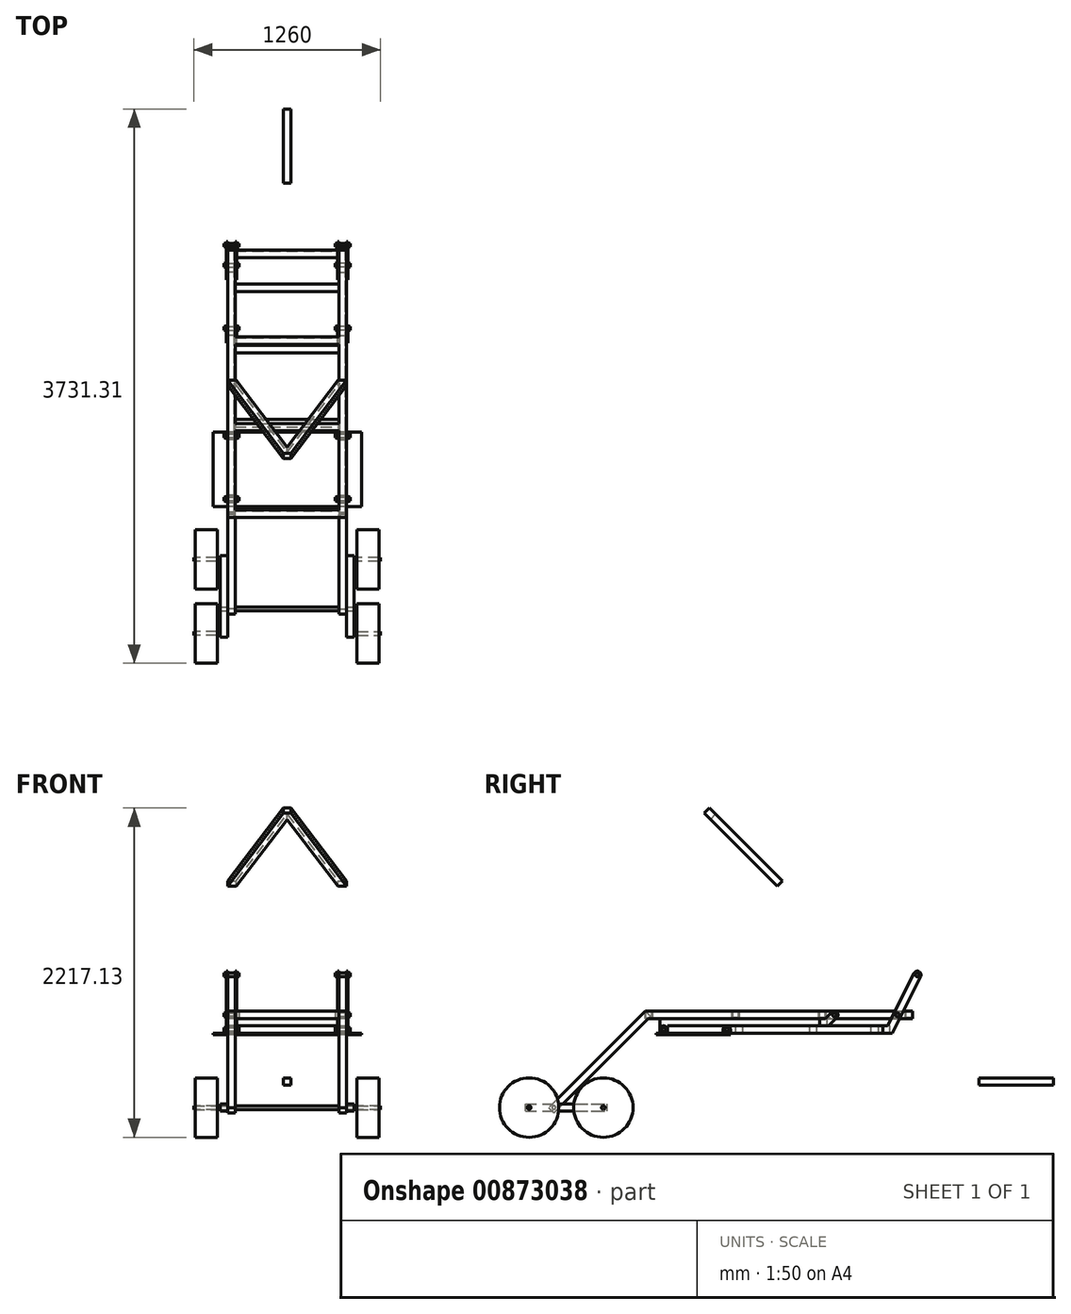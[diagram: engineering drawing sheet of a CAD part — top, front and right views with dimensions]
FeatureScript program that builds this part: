
annotation { "Feature Type Name" : "Feature", "Feature Type Description" : "" }
export const myFeature = defineFeature(function(context is Context, id is Id, definition is map)
    precondition{}
    {
        {
            assignVariable(context, id + "F0", {"name" : "TopLength", "anyValue" : 1800});
        }
        {
            assignVariable(context, id + "F1", {"name" : "TopWidth", "anyValue" : 800});
        }
        {
            assignVariable(context, id + "F2", {"name" : "PipeWidth", "anyValue" : 50});
        }
        {
            assignVariable(context, id + "F3", {"name" : "PipeThickness", "anyValue" : 5});
        }
        {
            var Q0;
            Q0=qCreatedBy(makeId("Front.planeOp"),FACE);
            var sketch = newSketch(context, id + "F4", { "sketchPlane" : qUnion([Q0])});
            skLineSegment(sketch, "E0.bottom", {"start": v(400, -25) * mm, "end": v(350, -25) * mm});
            skLineSegment(sketch, "E0.top", {"start": v(400, 25) * mm, "end": v(350, 25) * mm});
            skLineSegment(sketch, "E0.left", {"start": v(400, -25) * mm, "end": v(400, 25) * mm});
            skLineSegment(sketch, "E0.right", {"start": v(350, -25) * mm, "end": v(350, 25) * mm});
            skPoint(sketch, "E0.middle", {"position": v(375, 0) * mm});
            skSolve(sketch);
        }
        {
            var Q0;
            Q0 = qSketchRegion(id + "F4", true);
            extrude(context, id + "F5", {"entities" : qUnion([Q0]), "endBound" : BoundingType.SYMMETRIC, "depth" : (getVariable(context, 'TopLength')) * mm, "offsetDistance" : 25 * mm});
        }
        {
            var Q0;
            Q0=makeQuery(id+"F5.opExtrude","CAP_FACE",FACE,{"disambiguationData":[OSD([sQuery(id+"F4.wireOp",EDGE,"E0.bottom"),sQuery(id+"F4.wireOp",EDGE,"E0.top"),sQuery(id+"F4.wireOp",EDGE,"E0.left"),sQuery(id+"F4.wireOp",EDGE,"E0.right")])],"isStart":false});
            var Q1;
            Q1=makeQuery(id+"F5.opExtrude","CAP_FACE",FACE,{"disambiguationData":[OSD([sQuery(id+"F4.wireOp",EDGE,"E0.bottom"),sQuery(id+"F4.wireOp",EDGE,"E0.top"),sQuery(id+"F4.wireOp",EDGE,"E0.left"),sQuery(id+"F4.wireOp",EDGE,"E0.right")])],"isStart":true});
            shell(context, id + "F6", {"entities" : qUnion([Q0, Q1]), "thickness" : (getVariable(context, 'PipeThickness')) * mm});
        }
        {
            var Q0;
            Q0=makeQuery(id+"F5.opExtrude","SWEPT_BODY",BODY,{"disambiguationData":[OSD([sQuery(id+"F4.wireOp",EDGE,"E0.bottom"),sQuery(id+"F4.wireOp",EDGE,"E0.top"),sQuery(id+"F4.wireOp",EDGE,"E0.left"),sQuery(id+"F4.wireOp",EDGE,"E0.right")])]});
            var Q1;
            Q1=qCreatedBy(makeId("Right.planeOp"),FACE);
            mirror(context, id + "F7", {"entities" : qUnion([Q0]), "mirrorPlane" : qUnion([Q1])});
        }
        {
            var Q0;
            Q0=makeQuery(id+"F5.opExtrude","SWEPT_FACE",FACE,{"disambiguationData":[OSD([sQuery(id+"F4.wireOp",EDGE,"E0.right")])]});
            var sketch = newSketch(context, id + "F8", { "sketchPlane" : qUnion([Q0])});
            skLineSegment(sketch, "E1.bottom", {"start": v(900, 25) * mm, "end": v(850, 25) * mm});
            skLineSegment(sketch, "E1.top", {"start": v(900, -25) * mm, "end": v(850, -25) * mm});
            skLineSegment(sketch, "E1.left", {"start": v(900, 25) * mm, "end": v(900, -25) * mm});
            skLineSegment(sketch, "E1.right", {"start": v(850, 25) * mm, "end": v(850, -25) * mm});
            skLineSegment(sketch, "E2.bottom", {"start": v(855, 20) * mm, "end": v(895, 20) * mm});
            skLineSegment(sketch, "E2.top", {"start": v(855, -20) * mm, "end": v(895, -20) * mm});
            skLineSegment(sketch, "E2.left", {"start": v(855, 20) * mm, "end": v(855, -20) * mm});
            skLineSegment(sketch, "E2.right", {"start": v(895, 20) * mm, "end": v(895, -20) * mm});
            skLineSegment(sketch, "E3.1.0.0", {"start": v(271.67, -20) * mm, "end": v(311.67, -20) * mm});
            skLineSegment(sketch, "E3.1.0.1", {"start": v(311.67, 20) * mm, "end": v(311.67, -20) * mm});
            skLineSegment(sketch, "E3.1.0.2", {"start": v(316.67, 25) * mm, "end": v(266.67, 25) * mm});
            skLineSegment(sketch, "E3.1.0.3", {"start": v(316.67, 25) * mm, "end": v(316.67, -25) * mm});
            skLineSegment(sketch, "E3.1.0.4", {"start": v(271.67, 20) * mm, "end": v(311.67, 20) * mm});
            skLineSegment(sketch, "E3.1.0.5", {"start": v(316.67, -25) * mm, "end": v(266.67, -25) * mm});
            skLineSegment(sketch, "E3.1.0.6", {"start": v(271.67, 20) * mm, "end": v(271.67, -20) * mm});
            skLineSegment(sketch, "E3.1.0.7", {"start": v(266.67, 25) * mm, "end": v(266.67, -25) * mm});
            skLineSegment(sketch, "E3.2.0.0", {"start": v(-311.67, -20) * mm, "end": v(-271.67, -20) * mm});
            skLineSegment(sketch, "E3.2.0.1", {"start": v(-271.67, 20) * mm, "end": v(-271.67, -20) * mm});
            skLineSegment(sketch, "E3.2.0.2", {"start": v(-266.67, 25) * mm, "end": v(-316.67, 25) * mm});
            skLineSegment(sketch, "E3.2.0.3", {"start": v(-266.67, 25) * mm, "end": v(-266.67, -25) * mm});
            skLineSegment(sketch, "E3.2.0.4", {"start": v(-311.67, 20) * mm, "end": v(-271.67, 20) * mm});
            skLineSegment(sketch, "E3.2.0.5", {"start": v(-266.67, -25) * mm, "end": v(-316.67, -25) * mm});
            skLineSegment(sketch, "E3.2.0.6", {"start": v(-311.67, 20) * mm, "end": v(-311.67, -20) * mm});
            skLineSegment(sketch, "E3.2.0.7", {"start": v(-316.67, 25) * mm, "end": v(-316.67, -25) * mm});
            skLineSegment(sketch, "E3.3.0.0", {"start": v(-895, -20) * mm, "end": v(-855, -20) * mm});
            skLineSegment(sketch, "E3.3.0.1", {"start": v(-855, 20) * mm, "end": v(-855, -20) * mm});
            skLineSegment(sketch, "E3.3.0.2", {"start": v(-850, 25) * mm, "end": v(-900, 25) * mm});
            skLineSegment(sketch, "E3.3.0.3", {"start": v(-850, 25) * mm, "end": v(-850, -25) * mm});
            skLineSegment(sketch, "E3.3.0.4", {"start": v(-895, 20) * mm, "end": v(-855, 20) * mm});
            skLineSegment(sketch, "E3.3.0.5", {"start": v(-850, -25) * mm, "end": v(-900, -25) * mm});
            skLineSegment(sketch, "E3.3.0.6", {"start": v(-895, 20) * mm, "end": v(-895, -20) * mm});
            skLineSegment(sketch, "E3.3.0.7", {"start": v(-900, 25) * mm, "end": v(-900, -25) * mm});
            skLineSegment(sketch, "E3.direction1", {"start": v(850, -25) * mm, "end": v(266.67, -25) * mm, "construction": true});
            skSolve(sketch);
        }
        {
            var Q0;
            Q0 = qSketchRegion(id + "F8", true);
            extrude(context, id + "F9", {"entities" : qUnion([Q0]), "operationType" : NewBodyOperationType.ADD, "endBound" : BoundingType.UP_TO_NEXT, "depth" : 25 * mm, "offsetDistance" : 25 * mm});
        }
        {
            assignVariable(context, id + "F10", {"name" : "TopHeight", "anyValue" : 800});
        }
        {
            var Q0;
            Q0=makeQuery(id+"F7.opPattern","COPY",FACE,{"derivedFrom":makeQuery(id+"F5.opExtrude","SWEPT_FACE",FACE,{"disambiguationData":[OSD([sQuery(id+"F4.wireOp",EDGE,"E0.left")])]}),"instanceName":"1"});
            var sketch = newSketch(context, id + "F11", { "sketchPlane" : qUnion([Q0])});
            skLineSegment(sketch, "E4.bottom", {"start": v(-325, -25) * mm, "end": v(800, -25) * mm});
            skLineSegment(sketch, "E4.top", {"start": v(-325, -75) * mm, "end": v(800, -75) * mm});
            skLineSegment(sketch, "E4.left", {"start": v(-325, -25) * mm, "end": v(-325, -75) * mm});
            skLineSegment(sketch, "E4.right", {"start": v(800, -25) * mm, "end": v(800, -75) * mm});
            skCircle(sketch, "E5", {"center": v(-800, 0) * mm, "radius": 12.5 * mm, "construction": true});
            skCircle(sketch, "E6", {"center": v(-375, 0) * mm, "radius": 12.5 * mm, "construction": true});
            skCircle(sketch, "E7", {"center": v(775, -100) * mm, "radius": 12.5 * mm});
            skLineSegment(sketch, "E8.bottom", {"start": v(800, -75) * mm, "end": v(750, -75) * mm});
            skLineSegment(sketch, "E8.left", {"start": v(800, -75) * mm, "end": v(800, -100) * mm});
            skLineSegment(sketch, "E8.right", {"start": v(750, -75) * mm, "end": v(750, -100) * mm});
            skArc(sketch, "E9", {"start": v(750, -100) * mm, "mid": v(775, -125) * mm, "end": v(800, -100) * mm});
            skPoint(sketch, "E10.orphan", {"position": v(750, -125) * mm});
            skPoint(sketch, "E11.orphan", {"position": v(800, -125) * mm});
            skSolve(sketch);
        }
        {
            var Q0;
            {Q0=qUnion([makeQuery(id+"F11.imprint","IMPRINT",FACE,{"disambiguationData":[TD([[makeQuery(id+"F11.imprint","IMPRINT",EDGE,{"derivedFrom":sQuery(id+"F11.wireOp",EDGE,"E4.bottom")}),1.0]])]}),makeQuery(id+"F11.imprint","IMPRINT",FACE,{"disambiguationData":[TD([[makeQuery(id+"F11.imprint","IMPRINT",EDGE,{"derivedFrom":sQuery(id+"F11.wireOp",EDGE,"E7")}),-1.0]])]})]);}
            var Q1;
            Q1=makeQuery(id+"F9.boolean.opBoolean","SPLIT",FACE,{"disambiguationData":[TD([makeQuery(id+"F9.opExtrude","SWEPT_FACE",FACE,{"disambiguationData":[OSD([sQuery(id+"F8.wireOp",EDGE,"E3.1.0.7")])]})])],"derivedFrom":makeQuery(id+"F7.opPattern","COPY",FACE,{"derivedFrom":makeQuery(id+"F5.opExtrude","SWEPT_FACE",FACE,{"disambiguationData":[OSD([sQuery(id+"F4.wireOp",EDGE,"E0.right")])]}),"instanceName":"1"})});
            extrude(context, id + "F12", {"entities" : qUnion([Q0]), "endBound" : BoundingType.UP_TO_SURFACE, "oppositeDirection" : true, "depth" : 25 * mm, "endBoundEntityFace" : qUnion([Q1]), "offsetDistance" : 25 * mm});
        }
        {
            var Q0;
            Q0=makeQuery(id+"F7.opPattern","COPY",FACE,{"derivedFrom":makeQuery(id+"F5.opExtrude","SWEPT_FACE",FACE,{"disambiguationData":[OSD([sQuery(id+"F4.wireOp",EDGE,"E0.left")])]}),"instanceName":"1"});
            var sketch = newSketch(context, id + "F13", { "sketchPlane" : qUnion([Q0])});
            skCircle(sketch, "E12.0", {"center": v(775, -100) * mm, "radius": 12.5 * mm, "construction": true});
            skCircle(sketch, "E13", {"center": v(350, -100) * mm, "radius": 12.5 * mm});
            skCircle(sketch, "E14", {"center": v(-800, 0) * mm, "radius": 12.5 * mm, "construction": true});
            skLineSegment(sketch, "E15.bottom", {"start": v(350, -125) * mm, "end": v(-750, -125) * mm});
            skLineSegment(sketch, "E15.top", {"start": v(350, -75) * mm, "end": v(-750, -75) * mm});
            skLineSegment(sketch, "E15.right", {"start": v(-750, -125) * mm, "end": v(-750, -75) * mm});
            skPoint(sketch, "E15.middle", {"position": v(-187.5, -100) * mm});
            skCircle(sketch, "E16", {"center": v(-375, 0) * mm, "radius": 13.79 * mm, "construction": true});
            skArc(sketch, "E17", {"start": v(350, -75) * mm, "mid": v(375, -100) * mm, "end": v(350, -125) * mm});
            skPoint(sketch, "E18.orphan", {"position": v(375, -125) * mm});
            skPoint(sketch, "E19.orphan", {"position": v(375, -75) * mm});
            skSolve(sketch);
        }
        {
            var Q0;
            Q0 = qSketchRegion(id + "F13", true);
            var Q1;
            Q1=makeQuery(id+"F9.boolean.opBoolean","SPLIT",FACE,{"disambiguationData":[TD([makeQuery(id+"F9.opExtrude","SWEPT_FACE",FACE,{"disambiguationData":[OSD([sQuery(id+"F8.wireOp",EDGE,"E3.1.0.7")])]})])],"derivedFrom":makeQuery(id+"F7.opPattern","COPY",FACE,{"derivedFrom":makeQuery(id+"F5.opExtrude","SWEPT_FACE",FACE,{"disambiguationData":[OSD([sQuery(id+"F4.wireOp",EDGE,"E0.right")])]}),"instanceName":"1"})});
            extrude(context, id + "F14", {"entities" : qUnion([Q0]), "endBound" : BoundingType.UP_TO_SURFACE, "oppositeDirection" : true, "depth" : 25 * mm, "endBoundEntityFace" : qUnion([Q1]), "offsetDistance" : 25 * mm});
        }
        {
            var Q0;
            Q0=makeQuery(id+"F7.opPattern","COPY",FACE,{"derivedFrom":makeQuery(id+"F5.opExtrude","SWEPT_FACE",FACE,{"disambiguationData":[OSD([sQuery(id+"F4.wireOp",EDGE,"E0.left")])]}),"instanceName":"1"});
            var sketch = newSketch(context, id + "F15", { "sketchPlane" : qUnion([Q0])});
            skCircle(sketch, "E20", {"center": v(-800, 0) * mm, "radius": 12.5 * mm});
            skCircle(sketch, "E21", {"center": v(-375, 0) * mm, "radius": 12.5 * mm});
            skLineSegment(sketch, "E22", {"start": v(-275, -75) * mm, "end": v(-335.36, -75) * mm});
            skLineSegment(sketch, "E23", {"start": v(-335.36, -75) * mm, "end": v(-392.68, -17.68) * mm});
            skLineSegment(sketch, "E24", {"start": v(-357.32, 17.68) * mm, "end": v(-314.64, -25) * mm});
            skLineSegment(sketch, "E25", {"start": v(-314.64, -25) * mm, "end": v(-275, -25) * mm});
            skLineSegment(sketch, "E26", {"start": v(-275, -25) * mm, "end": v(-275, -75) * mm});
            skLineSegment(sketch, "E27", {"start": v(-375, 0) * mm, "end": v(-325, -50) * mm, "construction": true});
            skArc(sketch, "E28", {"start": v(-392.68, -17.68) * mm, "mid": v(-392.68, 17.68) * mm, "end": v(-357.32, 17.68) * mm});
            skLineSegment(sketch, "E29", {"start": v(-956.52, 257.15) * mm, "end": v(-765.45, -125) * mm});
            skLineSegment(sketch, "E30", {"start": v(-765.45, -125) * mm, "end": v(-700, -125) * mm});
            skLineSegment(sketch, "E31", {"start": v(-700, -125) * mm, "end": v(-700, -75) * mm});
            skLineSegment(sketch, "E32", {"start": v(-700, -75) * mm, "end": v(-734.55, -75) * mm});
            skLineSegment(sketch, "E33", {"start": v(-734.55, -75) * mm, "end": v(-911.8, 279.5) * mm});
            skCircle(sketch, "E34", {"center": v(-934.16, 268.33) * mm, "radius": 12.5 * mm});
            skArc(sketch, "E35", {"start": v(-911.8, 279.5) * mm, "mid": v(-945.34, 290.69) * mm, "end": v(-956.52, 257.15) * mm});
            skLineSegment(sketch, "E36", {"start": v(-800, 0) * mm, "end": v(-750, -100) * mm, "construction": true});
            skCircle(sketch, "E37.0", {"center": v(350, -100) * mm, "radius": 12.5 * mm, "construction": true});
            skCircle(sketch, "E38.0", {"center": v(775, -100) * mm, "radius": 12.5 * mm, "construction": true});
            skLineSegment(sketch, "E39", {"start": v(-800, 0) * mm, "end": v(350, -100) * mm, "construction": true});
            skLineSegment(sketch, "E40", {"start": v(-375, 0) * mm, "end": v(775, -100) * mm, "construction": true});
            skSolve(sketch);
        }
        {
            var Q0;
            Q0 = qSketchRegion(id + "F15", true);
            extrude(context, id + "F16", {"entities" : qUnion([Q0]), "depth" : 10 * mm, "offsetDistance" : 25 * mm});
        }
        {
            var Q0;
            Q0=makeQuery(id+"F7.opPattern","COPY",FACE,{"derivedFrom":makeQuery(id+"F5.opExtrude","SWEPT_FACE",FACE,{"disambiguationData":[OSD([sQuery(id+"F4.wireOp",EDGE,"E0.left")])]}),"instanceName":"1"});
            var Q1;
            Q1=makeQuery(id+"F9.boolean.opBoolean","SPLIT",FACE,{"disambiguationData":[TD([makeQuery(id+"F9.opExtrude","SWEPT_FACE",FACE,{"disambiguationData":[OSD([sQuery(id+"F8.wireOp",EDGE,"E3.2.0.7")])]})])],"derivedFrom":makeQuery(id+"F7.opPattern","COPY",FACE,{"derivedFrom":makeQuery(id+"F5.opExtrude","SWEPT_FACE",FACE,{"disambiguationData":[OSD([sQuery(id+"F4.wireOp",EDGE,"E0.right")])]}),"instanceName":"1"})});
            cPlane(context, id + "F17", {"entities" : qUnion([Q0, Q1]), "cplaneType" : CPlaneType.MID_PLANE, "offset" : 25 * mm, "width" : 150 * mm, "height" : 150 * mm});
        }
        {
            var Q0;
            Q0=makeQuery(id+"F16.opExtrude","SWEPT_BODY",BODY,{"disambiguationData":[OSD([sQuery(id+"F15.wireOp",EDGE,"E20"),sQuery(id+"F15.wireOp",EDGE,"E29"),sQuery(id+"F15.wireOp",EDGE,"E30"),sQuery(id+"F15.wireOp",EDGE,"E31"),sQuery(id+"F15.wireOp",EDGE,"E32"),sQuery(id+"F15.wireOp",EDGE,"E33"),sQuery(id+"F15.wireOp",EDGE,"E34"),sQuery(id+"F15.wireOp",EDGE,"E35")])]});
            var Q1;
            Q1=makeQuery(id+"F16.opExtrude","SWEPT_BODY",BODY,{"disambiguationData":[OSD([sQuery(id+"F15.wireOp",EDGE,"E21"),sQuery(id+"F15.wireOp",EDGE,"E22"),sQuery(id+"F15.wireOp",EDGE,"E23"),sQuery(id+"F15.wireOp",EDGE,"E24"),sQuery(id+"F15.wireOp",EDGE,"E26"),sQuery(id+"F15.wireOp",EDGE,"E25"),sQuery(id+"F15.wireOp",EDGE,"E28")])]});
            var Q2;
            Q2=qCreatedBy(id+"F17.planeOp",FACE);
            mirror(context, id + "F18", {"entities" : qUnion([Q0, Q1]), "mirrorPlane" : qUnion([Q2])});
        }
        {
            var Q0;
            Q0=makeQuery(id+"F16.opExtrude","CAP_FACE",FACE,{"disambiguationData":[OSD([sQuery(id+"F15.wireOp",EDGE,"E20"),sQuery(id+"F15.wireOp",EDGE,"E29"),sQuery(id+"F15.wireOp",EDGE,"E30"),sQuery(id+"F15.wireOp",EDGE,"E31"),sQuery(id+"F15.wireOp",EDGE,"E32"),sQuery(id+"F15.wireOp",EDGE,"E33"),sQuery(id+"F15.wireOp",EDGE,"E34"),sQuery(id+"F15.wireOp",EDGE,"E35")])],"isStart":false});
            var sketch = newSketch(context, id + "F19", { "sketchPlane" : qUnion([Q0])});
            skCircle(sketch, "E41.0", {"center": v(-800, 0) * mm, "radius": 12.5 * mm});
            skCircle(sketch, "E42.0", {"center": v(-375, 0) * mm, "radius": 12.5 * mm});
            skCircle(sketch, "E43.0", {"center": v(-934.16, 268.33) * mm, "radius": 12.5 * mm});
            skCircle(sketch, "E44.0", {"center": v(350, -100) * mm, "radius": 12.5 * mm});
            skCircle(sketch, "E45.0", {"center": v(775, -100) * mm, "radius": 12.5 * mm});
            skSolve(sketch);
        }
        {
            var Q0;
            Q0 = qSketchRegion(id + "F19", true);
            extrude(context, id + "F20", {"entities" : qUnion([Q0]), "depth" : 15 * mm, "offsetDistance" : 25 * mm, "hasSecondDirection" : true, "secondDirectionOppositeDirection" : true, "secondDirectionDepth" : (2 * 10 + 50 + 15) * mm});
        }
        {
            var Q0;
            Q0=makeQuery(id+"F14.opExtrude","SWEPT_FACE",FACE,{"disambiguationData":[OSD([sQuery(id+"F13.wireOp",EDGE,"E15.bottom")])]});
            var sketch = newSketch(context, id + "F21", { "sketchPlane" : qUnion([Q0])});
            skLineSegment(sketch, "E46.bottom", {"start": v(500, 325) * mm, "end": v(-500, 325) * mm});
            skLineSegment(sketch, "E46.top", {"start": v(500, 825) * mm, "end": v(-500, 825) * mm});
            skLineSegment(sketch, "E46.left", {"start": v(500, 325) * mm, "end": v(500, 825) * mm});
            skLineSegment(sketch, "E46.right", {"start": v(-500, 325) * mm, "end": v(-500, 825) * mm});
            skPoint(sketch, "E46.middle", {"position": v(0, 575) * mm});
            skSolve(sketch);
        }
        {
            var Q0;
            Q0 = qSketchRegion(id + "F21", true);
            extrude(context, id + "F22", {"entities" : qUnion([Q0]), "depth" : 10 * mm, "offsetDistance" : 25 * mm});
        }
        {
            var Q0;
            Q0=makeQuery(id+"F14.opExtrude","CAP_FACE",FACE,{"disambiguationData":[OSD([sQuery(id+"F13.wireOp",EDGE,"E13"),sQuery(id+"F13.wireOp",EDGE,"E15.bottom"),sQuery(id+"F13.wireOp",EDGE,"E15.top"),sQuery(id+"F13.wireOp",EDGE,"E15.right"),sQuery(id+"F13.wireOp",EDGE,"E17")])],"isStart":true});
            var sketch = newSketch(context, id + "F23", { "sketchPlane" : qUnion([Q0])});
            skCircle(sketch, "E47.0", {"center": v(350, -100) * mm, "radius": 12.5 * mm});
            skCircle(sketch, "E48.0", {"center": v(775, -100) * mm, "radius": 12.5 * mm});
            skLineSegment(sketch, "E49", {"start": v(325, -100) * mm, "end": v(325, -125) * mm});
            skLineSegment(sketch, "E50", {"start": v(325, -125) * mm, "end": v(375, -125) * mm});
            skLineSegment(sketch, "E51", {"start": v(375, -125) * mm, "end": v(375, -100) * mm});
            skLineSegment(sketch, "E52", {"start": v(750, -100) * mm, "end": v(750, -100) * mm});
            skLineSegment(sketch, "E53", {"start": v(800, -100) * mm, "end": v(800, -100) * mm});
            skArc(sketch, "E54", {"start": v(750, -100) * mm, "mid": v(775, -75) * mm, "end": v(800, -100) * mm});
            skArc(sketch, "E55", {"start": v(325, -100) * mm, "mid": v(350, -75) * mm, "end": v(375, -100) * mm});
            skLineSegment(sketch, "E56", {"start": v(750, -100) * mm, "end": v(750, -125) * mm});
            skLineSegment(sketch, "E57", {"start": v(750, -125) * mm, "end": v(800, -125) * mm});
            skLineSegment(sketch, "E58", {"start": v(800, -125) * mm, "end": v(800, -100) * mm});
            skSolve(sketch);
        }
        {
            var Q0;
            Q0 = qSketchRegion(id + "F23", true);
            extrude(context, id + "F24", {"entities" : qUnion([Q0]), "depth" : 10 * mm, "offsetDistance" : 25 * mm});
        }
        {
            var Q0;
            Q0=makeQuery(id+"F24.opExtrude","SWEPT_BODY",BODY,{"disambiguationData":[OSD([sQuery(id+"F23.wireOp",EDGE,"E47.0"),sQuery(id+"F23.wireOp",EDGE,"E49"),sQuery(id+"F23.wireOp",EDGE,"E50"),sQuery(id+"F23.wireOp",EDGE,"E51"),sQuery(id+"F23.wireOp",EDGE,"E55")])]});
            var Q1;
            Q1=makeQuery(id+"F24.opExtrude","SWEPT_BODY",BODY,{"disambiguationData":[OSD([sQuery(id+"F23.wireOp",EDGE,"E48.0"),sQuery(id+"F23.wireOp",EDGE,"E52"),sQuery(id+"F23.wireOp",EDGE,"6jW9iRk8-fZLG-PZQX-P5f5-OUHjVVszkgpw"),sQuery(id+"F23.wireOp",EDGE,"E53"),sQuery(id+"F23.wireOp",EDGE,"E54")])]});
            var Q2;
            Q2=qCreatedBy(id+"F17.planeOp",FACE);
            mirror(context, id + "F25", {"entities" : qUnion([Q0, Q1]), "mirrorPlane" : qUnion([Q2])});
        }
        {
            var Q0;
            Q0=makeQuery(id+"F20.opExtrude","SWEPT_BODY",BODY,{"disambiguationData":[OSD([sQuery(id+"F19.wireOp",EDGE,"E43.0")])]});
            var Q1;
            Q1=makeQuery(id+"F20.opExtrude","SWEPT_BODY",BODY,{"disambiguationData":[OSD([sQuery(id+"F19.wireOp",EDGE,"E41.0")])]});
            var Q2;
            Q2=makeQuery(id+"F20.opExtrude","SWEPT_BODY",BODY,{"disambiguationData":[OSD([sQuery(id+"F19.wireOp",EDGE,"E42.0")])]});
            var Q3;
            Q3=makeQuery(id+"F20.opExtrude","SWEPT_BODY",BODY,{"disambiguationData":[OSD([sQuery(id+"F19.wireOp",EDGE,"E44.0")])]});
            var Q4;
            Q4=makeQuery(id+"F20.opExtrude","SWEPT_BODY",BODY,{"disambiguationData":[OSD([sQuery(id+"F19.wireOp",EDGE,"E45.0")])]});
            var Q5;
            Q5=makeQuery(id+"F16.opExtrude","SWEPT_BODY",BODY,{"disambiguationData":[OSD([sQuery(id+"F15.wireOp",EDGE,"E20"),sQuery(id+"F15.wireOp",EDGE,"E29"),sQuery(id+"F15.wireOp",EDGE,"E30"),sQuery(id+"F15.wireOp",EDGE,"E31"),sQuery(id+"F15.wireOp",EDGE,"E32"),sQuery(id+"F15.wireOp",EDGE,"E33"),sQuery(id+"F15.wireOp",EDGE,"E34"),sQuery(id+"F15.wireOp",EDGE,"E35")])]});
            var Q6;
            Q6=makeQuery(id+"F18.opPattern","COPY",BODY,{"derivedFrom":makeQuery(id+"F16.opExtrude","SWEPT_BODY",BODY,{"disambiguationData":[OSD([sQuery(id+"F15.wireOp",EDGE,"E20"),sQuery(id+"F15.wireOp",EDGE,"E29"),sQuery(id+"F15.wireOp",EDGE,"E30"),sQuery(id+"F15.wireOp",EDGE,"E31"),sQuery(id+"F15.wireOp",EDGE,"E32"),sQuery(id+"F15.wireOp",EDGE,"E33"),sQuery(id+"F15.wireOp",EDGE,"E34"),sQuery(id+"F15.wireOp",EDGE,"E35")])]}),"instanceName":"1"});
            var Q7;
            Q7=makeQuery(id+"F16.opExtrude","SWEPT_BODY",BODY,{"disambiguationData":[OSD([sQuery(id+"F15.wireOp",EDGE,"E21"),sQuery(id+"F15.wireOp",EDGE,"E22"),sQuery(id+"F15.wireOp",EDGE,"E23"),sQuery(id+"F15.wireOp",EDGE,"E24"),sQuery(id+"F15.wireOp",EDGE,"E26"),sQuery(id+"F15.wireOp",EDGE,"E25"),sQuery(id+"F15.wireOp",EDGE,"E28")])]});
            var Q8;
            Q8=makeQuery(id+"F18.opPattern","COPY",BODY,{"derivedFrom":makeQuery(id+"F16.opExtrude","SWEPT_BODY",BODY,{"disambiguationData":[OSD([sQuery(id+"F15.wireOp",EDGE,"E21"),sQuery(id+"F15.wireOp",EDGE,"E22"),sQuery(id+"F15.wireOp",EDGE,"E23"),sQuery(id+"F15.wireOp",EDGE,"E24"),sQuery(id+"F15.wireOp",EDGE,"E26"),sQuery(id+"F15.wireOp",EDGE,"E25"),sQuery(id+"F15.wireOp",EDGE,"E28")])]}),"instanceName":"1"});
            var Q9;
            Q9=makeQuery(id+"F14.opExtrude","SWEPT_BODY",BODY,{"disambiguationData":[OSD([sQuery(id+"F13.wireOp",EDGE,"E13"),sQuery(id+"F13.wireOp",EDGE,"E15.bottom"),sQuery(id+"F13.wireOp",EDGE,"E15.top"),sQuery(id+"F13.wireOp",EDGE,"E15.right"),sQuery(id+"F13.wireOp",EDGE,"E17")])]});
            var Q10;
            Q10=makeQuery(id+"F12.opExtrude","SWEPT_BODY",BODY,{"disambiguationData":[OSD([sQuery(id+"F11.wireOp",EDGE,"E4.bottom"),sQuery(id+"F11.wireOp",EDGE,"E4.top"),sQuery(id+"F11.wireOp",EDGE,"E4.left"),sQuery(id+"F11.wireOp",EDGE,"E4.right"),sQuery(id+"F11.wireOp",EDGE,"E7"),sQuery(id+"F11.wireOp",EDGE,"E8.left"),sQuery(id+"F11.wireOp",EDGE,"E8.right"),sQuery(id+"F11.wireOp",EDGE,"E9")])]});
            var Q11;
            Q11=makeQuery(id+"F24.opExtrude","SWEPT_BODY",BODY,{"disambiguationData":[OSD([sQuery(id+"F23.wireOp",EDGE,"E47.0"),sQuery(id+"F23.wireOp",EDGE,"E49"),sQuery(id+"F23.wireOp",EDGE,"E50"),sQuery(id+"F23.wireOp",EDGE,"E51"),sQuery(id+"F23.wireOp",EDGE,"E55")])]});
            var Q12;
            Q12=makeQuery(id+"F25.opPattern","COPY",BODY,{"derivedFrom":makeQuery(id+"F24.opExtrude","SWEPT_BODY",BODY,{"disambiguationData":[OSD([sQuery(id+"F23.wireOp",EDGE,"E47.0"),sQuery(id+"F23.wireOp",EDGE,"E49"),sQuery(id+"F23.wireOp",EDGE,"E50"),sQuery(id+"F23.wireOp",EDGE,"E51"),sQuery(id+"F23.wireOp",EDGE,"E55")])]}),"instanceName":"1"});
            var Q13;
            Q13=makeQuery(id+"F24.opExtrude","SWEPT_BODY",BODY,{"disambiguationData":[OSD([sQuery(id+"F23.wireOp",EDGE,"E48.0"),sQuery(id+"F23.wireOp",EDGE,"E52"),sQuery(id+"F23.wireOp",EDGE,"6jW9iRk8-fZLG-PZQX-P5f5-OUHjVVszkgpw"),sQuery(id+"F23.wireOp",EDGE,"E53"),sQuery(id+"F23.wireOp",EDGE,"E54")])]});
            var Q14;
            Q14=makeQuery(id+"F25.opPattern","COPY",BODY,{"derivedFrom":makeQuery(id+"F24.opExtrude","SWEPT_BODY",BODY,{"disambiguationData":[OSD([sQuery(id+"F23.wireOp",EDGE,"E48.0"),sQuery(id+"F23.wireOp",EDGE,"E52"),sQuery(id+"F23.wireOp",EDGE,"6jW9iRk8-fZLG-PZQX-P5f5-OUHjVVszkgpw"),sQuery(id+"F23.wireOp",EDGE,"E53"),sQuery(id+"F23.wireOp",EDGE,"E54")])]}),"instanceName":"1"});
            var Q15;
            Q15=qCreatedBy(makeId("Right.planeOp"),FACE);
            mirror(context, id + "F26", {"entities" : qUnion([Q0, Q1, Q2, Q3, Q4, Q5, Q6, Q7, Q8, Q9, Q10, Q11, Q12, Q13, Q14]), "mirrorPlane" : qUnion([Q15])});
        }
        {
            var Q0;
            {var subQ0=makeQuery(id+"F5.opExtrude","SWEPT_FACE",FACE,{"disambiguationData":[OSD([sQuery(id+"F4.wireOp",EDGE,"E0.bottom")])]});Q0=makeQuery(id+"F9.boolean.opBoolean","MERGE",FACE,{"derivedFrom":[subQ0,makeQuery(id+"F7.opPattern","COPY",FACE,{"derivedFrom":subQ0,"instanceName":"1"}),makeQuery(id+"F9.opExtrude","SWEPT_FACE",FACE,{"disambiguationData":[OSD([sQuery(id+"F8.wireOp",EDGE,"E1.top")])]}),makeQuery(id+"F9.opExtrude","SWEPT_FACE",FACE,{"disambiguationData":[OSD([sQuery(id+"F8.wireOp",EDGE,"E3.1.0.5")])]}),makeQuery(id+"F9.opExtrude","SWEPT_FACE",FACE,{"disambiguationData":[OSD([sQuery(id+"F8.wireOp",EDGE,"E3.2.0.5")])]}),makeQuery(id+"F9.opExtrude","SWEPT_FACE",FACE,{"disambiguationData":[OSD([sQuery(id+"F8.wireOp",EDGE,"E3.3.0.5")])]})]});}
            cPlane(context, id + "F27", {"entities" : qUnion([Q0]), "cplaneType" : CPlaneType.OFFSET, "offset" : (getVariable(context, 'TopHeight')) * mm, "width" : 150 * mm, "height" : 150 * mm});
        }
        {
            var Q0;
            Q0=makeQuery(id+"F7.opPattern","COPY",FACE,{"derivedFrom":makeQuery(id+"F5.opExtrude","SWEPT_FACE",FACE,{"disambiguationData":[OSD([sQuery(id+"F4.wireOp",EDGE,"E0.left")])]}),"instanceName":"1"});
            var sketch = newSketch(context, id + "F28", { "sketchPlane" : qUnion([Q0])});
            skLineSegment(sketch, "E59", {"start": v(900, 25) * mm, "end": v(1550, -625) * mm});
            skLineSegment(sketch, "E60", {"start": v(1550, -625) * mm, "end": v(1514.64, -660.36) * mm});
            skLineSegment(sketch, "E61", {"start": v(1514.64, -660.36) * mm, "end": v(864.64, -10.36) * mm});
            skLineSegment(sketch, "E62", {"start": v(864.64, -10.36) * mm, "end": v(900, 25) * mm});
            skCircle(sketch, "E63", {"center": v(1092.75, -625) * mm, "radius": 200 * mm, "construction": true});
            skCircle(sketch, "E64", {"center": v(1592.75, -625) * mm, "radius": 200 * mm, "construction": true});
            skCircle(sketch, "E65", {"center": v(1514.64, -625) * mm, "radius": 12.5 * mm});
            skLineSegment(sketch, "E66", {"start": v(1514.64, -625) * mm, "end": v(1567.24, -677.6) * mm, "construction": true});
            skSolve(sketch);
        }
        {
            var Q0;
            Q0 = qSketchRegion(id + "F28", true);
            extrude(context, id + "F29", {"entities" : qUnion([Q0]), "oppositeDirection" : true, "depth" : (getVariable(context, 'PipeWidth')) * mm, "offsetDistance" : 25 * mm});
        }
        {
            var Q0;
            Q0=makeQuery(id+"F29.opExtrude","SWEPT_BODY",BODY,{"disambiguationData":[OSD([sQuery(id+"F28.wireOp",EDGE,"E59"),sQuery(id+"F28.wireOp",EDGE,"E60"),sQuery(id+"F28.wireOp",EDGE,"E61"),sQuery(id+"F28.wireOp",EDGE,"E62"),sQuery(id+"F28.wireOp",EDGE,"E65")])]});
            var Q1;
            Q1=qCreatedBy(makeId("Right.planeOp"),FACE);
            mirror(context, id + "F30", {"operationType" : NewBodyOperationType.ADD, "entities" : qUnion([Q0]), "mirrorPlane" : qUnion([Q1])});
        }
        {
            var Q0;
            Q0=makeQuery(id+"F30.boolean.opBoolean","MERGE",FACE,{"derivedFrom":[makeQuery(id+"F7.opPattern","COPY",FACE,{"derivedFrom":makeQuery(id+"F5.opExtrude","SWEPT_FACE",FACE,{"disambiguationData":[OSD([sQuery(id+"F4.wireOp",EDGE,"E0.left")])]}),"instanceName":"1"}),makeQuery(id+"F29.opExtrude","CAP_FACE",FACE,{"disambiguationData":[OSD([sQuery(id+"F28.wireOp",EDGE,"E59"),sQuery(id+"F28.wireOp",EDGE,"E60"),sQuery(id+"F28.wireOp",EDGE,"E61"),sQuery(id+"F28.wireOp",EDGE,"E62"),sQuery(id+"F28.wireOp",EDGE,"E65")])],"isStart":true})]});
            var sketch = newSketch(context, id + "F31", { "sketchPlane" : qUnion([Q0])});
            skCircle(sketch, "E67.0", {"center": v(1514.64, -625) * mm, "radius": 12.5 * mm});
            skSolve(sketch);
        }
        {
            var Q0;
            Q0 = qSketchRegion(id + "F31", true);
            extrude(context, id + "F32", {"entities" : qUnion([Q0]), "operationType" : NewBodyOperationType.ADD, "depth" : (50 + 15) * mm, "offsetDistance" : 25 * mm, "hasSecondDirection" : true, "secondDirectionOppositeDirection" : true, "secondDirectionDepth" : (getVariable(context, 'TopWidth') + getVariable(context, 'PipeWidth') + 15) * mm});
        }
        {
            var Q0;
            Q0=makeQuery(id+"F30.boolean.opBoolean","MERGE",FACE,{"derivedFrom":[makeQuery(id+"F7.opPattern","COPY",FACE,{"derivedFrom":makeQuery(id+"F5.opExtrude","SWEPT_FACE",FACE,{"disambiguationData":[OSD([sQuery(id+"F4.wireOp",EDGE,"E0.left")])]}),"instanceName":"1"}),makeQuery(id+"F29.opExtrude","CAP_FACE",FACE,{"disambiguationData":[OSD([sQuery(id+"F28.wireOp",EDGE,"E59"),sQuery(id+"F28.wireOp",EDGE,"E60"),sQuery(id+"F28.wireOp",EDGE,"E61"),sQuery(id+"F28.wireOp",EDGE,"E62"),sQuery(id+"F28.wireOp",EDGE,"E65")])],"isStart":true})]});
            var sketch = newSketch(context, id + "F33", { "sketchPlane" : qUnion([Q0])});
            skCircle(sketch, "E68.0.0", {"center": v(1514.64, -625) * mm, "radius": 12.5 * mm});
            skLineSegment(sketch, "E69.bottom", {"start": v(1706.31, -650) * mm, "end": v(1156.31, -650) * mm});
            skLineSegment(sketch, "E69.top", {"start": v(1706.31, -600) * mm, "end": v(1156.31, -600) * mm});
            skLineSegment(sketch, "E69.left", {"start": v(1706.31, -650) * mm, "end": v(1706.31, -600) * mm});
            skLineSegment(sketch, "E69.right", {"start": v(1156.31, -650) * mm, "end": v(1156.31, -600) * mm});
            skPoint(sketch, "E69.middle", {"position": v(1431.31, -625) * mm});
            skCircle(sketch, "E70", {"center": v(1681.31, -625) * mm, "radius": 12.5 * mm});
            skCircle(sketch, "E71", {"center": v(1181.31, -625) * mm, "radius": 12.5 * mm});
            skSolve(sketch);
        }
        {
            var Q0;
            Q0 = qSketchRegion(id + "F33", true);
            extrude(context, id + "F34", {"entities" : qUnion([Q0]), "depth" : (getVariable(context, 'PipeWidth')) * mm, "offsetDistance" : 25 * mm});
        }
        {
            var Q0;
            Q0=makeQuery(id+"F34.opExtrude","CAP_FACE",FACE,{"disambiguationData":[OSD([sQuery(id+"F33.wireOp",EDGE,"E68.0.0"),sQuery(id+"F33.wireOp",EDGE,"E69.bottom"),sQuery(id+"F33.wireOp",EDGE,"E69.top"),sQuery(id+"F33.wireOp",EDGE,"E69.left"),sQuery(id+"F33.wireOp",EDGE,"E69.right"),sQuery(id+"F33.wireOp",EDGE,"E70"),sQuery(id+"F33.wireOp",EDGE,"E71")])],"isStart":false});
            var sketch = newSketch(context, id + "F35", { "sketchPlane" : qUnion([Q0])});
            skCircle(sketch, "E72.0", {"center": v(1681.31, -625) * mm, "radius": 12.5 * mm});
            skCircle(sketch, "E73.0", {"center": v(1181.31, -625) * mm, "radius": 12.5 * mm});
            skSolve(sketch);
        }
        {
            var Q0;
            Q0 = qSketchRegion(id + "F35", true);
            var Q1;
            Q1=makeQuery(id+"F34.opExtrude","CAP_FACE",FACE,{"disambiguationData":[OSD([sQuery(id+"F33.wireOp",EDGE,"E68.0.0"),sQuery(id+"F33.wireOp",EDGE,"E69.bottom"),sQuery(id+"F33.wireOp",EDGE,"E69.top"),sQuery(id+"F33.wireOp",EDGE,"E69.left"),sQuery(id+"F33.wireOp",EDGE,"E69.right"),sQuery(id+"F33.wireOp",EDGE,"E70"),sQuery(id+"F33.wireOp",EDGE,"E71")])],"isStart":true});
            extrude(context, id + "F36", {"entities" : qUnion([Q0]), "operationType" : NewBodyOperationType.ADD, "depth" : (20 + 150 + 10) * mm, "offsetDistance" : 25 * mm, "hasSecondDirection" : true, "secondDirectionBound" : SecondDirectionBoundingType.UP_TO_SURFACE, "secondDirectionOppositeDirection" : true, "secondDirectionDepth" : 25 * mm, "secondDirectionBoundEntityFace" : qUnion([Q1])});
        }
        {
            var Q0;
            Q0=makeQuery(id+"F36.opExtrude","CAP_FACE",FACE,{"disambiguationData":[OSD([sQuery(id+"F35.wireOp",EDGE,"E73.0")])],"isStart":false});
            cPlane(context, id + "F37", {"entities" : qUnion([Q0]), "cplaneType" : CPlaneType.OFFSET, "offset" : 10 * mm, "oppositeDirection" : true, "width" : 150 * mm, "height" : 150 * mm});
        }
        {
            var Q0;
            Q0=qCreatedBy(id+"F37.planeOp",FACE);
            var sketch = newSketch(context, id + "F38", { "sketchPlane" : qUnion([Q0])});
            skCircle(sketch, "E74.0", {"center": v(1181.31, -625) * mm, "radius": 12.5 * mm});
            skCircle(sketch, "E75.0.0", {"center": v(1681.31, -625) * mm, "radius": 12.5 * mm});
            skCircle(sketch, "E76", {"center": v(1181.31, -625) * mm, "radius": 200 * mm});
            skCircle(sketch, "E77", {"center": v(1681.31, -625) * mm, "radius": 200 * mm});
            skSolve(sketch);
        }
        {
            var Q0;
            Q0 = qSketchRegion(id + "F38", true);
            extrude(context, id + "F39", {"entities" : qUnion([Q0]), "oppositeDirection" : true, "depth" : 150 * mm, "offsetDistance" : 25 * mm});
        }
        {
            var Q0;
            Q0=makeQuery(id+"F39.opExtrude","SWEPT_BODY",BODY,{"disambiguationData":[OSD([sQuery(id+"F38.wireOp",EDGE,"E74.0"),sQuery(id+"F38.wireOp",EDGE,"E76")])]});
            var Q1;
            Q1=makeQuery(id+"F39.opExtrude","SWEPT_BODY",BODY,{"disambiguationData":[OSD([sQuery(id+"F38.wireOp",EDGE,"E75.0.0"),sQuery(id+"F38.wireOp",EDGE,"E77")])]});
            var Q2;
            Q2=makeQuery(id+"F34.opExtrude","SWEPT_BODY",BODY,{"disambiguationData":[OSD([sQuery(id+"F33.wireOp",EDGE,"E68.0.0"),sQuery(id+"F33.wireOp",EDGE,"E69.bottom"),sQuery(id+"F33.wireOp",EDGE,"E69.top"),sQuery(id+"F33.wireOp",EDGE,"E69.left"),sQuery(id+"F33.wireOp",EDGE,"E69.right"),sQuery(id+"F33.wireOp",EDGE,"E70"),sQuery(id+"F33.wireOp",EDGE,"E71")])]});
            var Q3;
            Q3=qCreatedBy(makeId("Right.planeOp"),FACE);
            mirror(context, id + "F40", {"entities" : qUnion([Q0, Q1, Q2]), "mirrorPlane" : qUnion([Q3])});
        }
        {
            var Q0;
            Q0=makeQuery(id+"F26.opPattern","COPY",FACE,{"derivedFrom":makeQuery(id+"F14.opExtrude","CAP_FACE",FACE,{"disambiguationData":[OSD([sQuery(id+"F13.wireOp",EDGE,"E13"),sQuery(id+"F13.wireOp",EDGE,"E15.bottom"),sQuery(id+"F13.wireOp",EDGE,"E15.top"),sQuery(id+"F13.wireOp",EDGE,"E15.right"),sQuery(id+"F13.wireOp",EDGE,"E17")])],"isStart":false}),"instanceName":"1"});
            var sketch = newSketch(context, id + "F41", { "sketchPlane" : qUnion([Q0])});
            skLineSegment(sketch, "E78.bottom", {"start": v(-672.16, -75) * mm, "end": v(-622.16, -75) * mm});
            skLineSegment(sketch, "E78.top", {"start": v(-672.16, -125) * mm, "end": v(-622.16, -125) * mm});
            skLineSegment(sketch, "E78.left", {"start": v(-672.16, -75) * mm, "end": v(-672.16, -125) * mm});
            skLineSegment(sketch, "E78.right", {"start": v(-622.16, -75) * mm, "end": v(-622.16, -125) * mm});
            skLineSegment(sketch, "E79.bottom", {"start": v(290.37, -75) * mm, "end": v(240.37, -75) * mm});
            skLineSegment(sketch, "E79.top", {"start": v(290.37, -125) * mm, "end": v(240.37, -125) * mm});
            skLineSegment(sketch, "E79.left", {"start": v(290.37, -75) * mm, "end": v(290.37, -125) * mm});
            skLineSegment(sketch, "E79.right", {"start": v(240.37, -75) * mm, "end": v(240.37, -125) * mm});
            skLineSegment(sketch, "E80.bottom", {"start": v(-208.34, -75) * mm, "end": v(-258.34, -75) * mm});
            skLineSegment(sketch, "E80.top", {"start": v(-208.34, -125) * mm, "end": v(-258.34, -125) * mm});
            skLineSegment(sketch, "E80.left", {"start": v(-208.34, -75) * mm, "end": v(-208.34, -125) * mm});
            skLineSegment(sketch, "E80.right", {"start": v(-258.34, -75) * mm, "end": v(-258.34, -125) * mm});
            skSolve(sketch);
        }
        {
            var Q0;
            Q0 = qSketchRegion(id + "F41", true);
            extrude(context, id + "F42", {"entities" : qUnion([Q0]), "endBound" : BoundingType.UP_TO_NEXT, "depth" : 25 * mm, "offsetDistance" : 25 * mm});
        }
        {
            var Q0;
            Q0=qCreatedBy(makeId("Right.planeOp"),FACE);
            var sketch = newSketch(context, id + "F43", { "sketchPlane" : qUnion([Q0])});
            skLineSegment(sketch, "E81.bottom", {"start": v(1850, -425) * mm, "end": v(1350, -425) * mm});
            skLineSegment(sketch, "E81.top", {"start": v(1850, -475) * mm, "end": v(1350, -475) * mm});
            skLineSegment(sketch, "E81.left", {"start": v(1850, -425) * mm, "end": v(1850, -475) * mm});
            skLineSegment(sketch, "E81.right", {"start": v(1350, -425) * mm, "end": v(1350, -475) * mm});
            skLineSegment(sketch, "E82", {"start": v(1350, -425) * mm, "end": v(900, 25) * mm, "construction": true});
            skSolve(sketch);
        }
        {
            var Q0;
            Q0 = qSketchRegion(id + "F43", true);
            extrude(context, id + "F44", {"entities" : qUnion([Q0]), "endBound" : BoundingType.SYMMETRIC, "depth" : (getVariable(context, 'PipeWidth')) * mm, "offsetDistance" : 25 * mm});
        }
        {
            var Q0;
            Q0=makeQuery(id+"F5.opExtrude","CAP_VERTEX",VERTEX,{"disambiguationData":[OSD([sQuery(id+"F4.wireOp",EDGE,"E0.top"),sQuery(id+"F4.wireOp",EDGE,"E0.left")])],"isStart":true});
            var Q1;
            Q1=makeQuery(id+"F7.opPattern","COPY",VERTEX,{"derivedFrom":makeQuery(id+"F5.opExtrude","CAP_VERTEX",VERTEX,{"disambiguationData":[OSD([sQuery(id+"F4.wireOp",EDGE,"E0.top"),sQuery(id+"F4.wireOp",EDGE,"E0.left")])],"isStart":true}),"instanceName":"1"});
            var Q2;
            Q2=makeQuery(id+"F44.opExtrude","CAP_VERTEX",VERTEX,{"disambiguationData":[OSD([sQuery(id+"F43.wireOp",EDGE,"E81.bottom"),sQuery(id+"F43.wireOp",EDGE,"E81.right")])],"isStart":true});
            cPlane(context, id + "F45", {"entities" : qUnion([Q0, Q1, Q2]), "cplaneType" : CPlaneType.THREE_POINT, "offset" : 25 * mm, "width" : 150 * mm, "height" : 150 * mm});
        }
        {
            var Q0;
            Q0=qCreatedBy(id+"F45.planeOp",FACE);
            var sketch = newSketch(context, id + "F46", { "sketchPlane" : qUnion([Q0])});
            skLineSegment(sketch, "E83", {"start": v(400, 618.72) * mm, "end": v(25, 1314.7) * mm});
            skLineSegment(sketch, "E84", {"start": v(25, 1314.7) * mm, "end": v(-25, 1314.7) * mm});
            skLineSegment(sketch, "E85", {"start": v(-25, 1314.7) * mm, "end": v(-400, 618.72) * mm});
            skLineSegment(sketch, "E86", {"start": v(400, 618.72) * mm, "end": v(343.2, 618.72) * mm});
            skLineSegment(sketch, "E87", {"start": v(343.2, 618.72) * mm, "end": v(0, 1255.7) * mm});
            skLineSegment(sketch, "E88", {"start": v(0, 1255.7) * mm, "end": v(-343.2, 618.72) * mm});
            skLineSegment(sketch, "E89", {"start": v(-343.2, 618.72) * mm, "end": v(-400, 618.72) * mm});
            skSolve(sketch);
        }
        {
            var Q0;
            Q0 = qSketchRegion(id + "F46", true);
            extrude(context, id + "F47", {"entities" : qUnion([Q0]), "oppositeDirection" : true, "depth" : 50 * mm, "offsetDistance" : 25 * mm});
        }
    });
